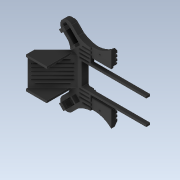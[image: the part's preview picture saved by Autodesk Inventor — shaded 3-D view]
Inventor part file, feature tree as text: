
AUTODESK INVENTOR PART (.ipt)
format: ipt  version: 2020 (Build 240168000, 168)  size: 2,749,440 bytes
history: native  units: mm
features: projected_geometry x46, extrude x34, sketch x34, reference x22, other x20, chamfer x10, plane x4, hole x3, move_body x3, direct_edit x2, emboss x1
ambient origin geometry x8: Origin, YZ Plane, XZ Plane, XY Plane, X Axis, Y Axis, Z Axis, Center Point
bodies: Solid1 (feature_tree)
feature tree (179):
  extrude  "Extrusion1"  Depth=4.404mm
  extrude  "Extrusion2"  Depth=22.0mm
  extrude  "Extrusion3"  Depth=35.3mm
  hole  "Hole2"  [1 undecoded]
  extrude  "Extrusion10"  Depth=19.0mm
  extrude  "Extrusion17"  Depth=10.0mm
  sketch  "Sketch27"  dims[d12=19.0mm d13=100.0mm]
  hole  "Hole4"  [1 undecoded]
  extrude  "Extrusion29"  Depth=17.453293mm
  extrude  "Extrusion30"  Depth=13.962634mm
  extrude  "Extrusion31"  Depth=4.8mm
  extrude  "Extrusion34"  Depth=6.2mm
  plane  "Work Plane1"
  extrude  "Extrusion42"  Depth=2.5mm
  hole  "Hole6"  [1 undecoded]
  extrude  "Extrusion46"  Depth=2.0mm
  chamfer  "Chamfer13"  Distance=2.0mm
  chamfer  "Chamfer14"  Distance=2.0mm
  chamfer  "Chamfer15"  Distance=4.8mm
  chamfer  "Chamfer16"  Distance=33.0mm
  chamfer  "Chamfer17"  Distance=2.5mm
  chamfer  "Chamfer18"  Distance=2.0mm
  extrude  "Extrusion54"  Depth=0.5mm
  chamfer  "Chamfer19"  Distance=2.0mm
  extrude  "Extrusion55"  Depth=14.0mm
  plane  "Work Plane2"
  extrude  "Extrusion57"  Depth=0.5mm
  direct_edit  "Direct Edit5"
  direct_edit  "Direct Edit6"
  plane  "Work Plane3"
  extrude  "Extrusion58"  Depth=0.5mm
  sketch  "Sketch59"  dims[d30=6.2mm]
  extrude  "Extrusion59"  Depth=0.5mm
  extrude  "Extrusion60"  Depth=10.0mm TaperAngle=0.0deg
  chamfer  "Chamfer21"  Distance=146.583126mm
  extrude  "Extrusion61"  Depth=0.5mm
  extrude  "Extrusion62"  Depth=0.5mm
  extrude  "Extrusion63"  Depth=0.5mm
  extrude  "Extrusion64"  Depth=0.5mm
  sketch  "Sketch65"  dims[d37=6.2mm]
  plane  "Work Plane4"
  extrude  "Extrusion65"  Depth=0.5mm
  extrude  "Extrusion66"  Depth=0.5mm
  extrude  "Extrusion68"  Depth=0.5mm
  extrude  "Extrusion69"  Depth=0.5mm
  extrude  "Extrusion71"  Depth=0.5mm
  extrude  "Extrusion84"  Depth=0.5mm
  chamfer  "Chamfer24"  Distance=142.600153mm
  extrude  "Extrusion87"  Depth=0.5mm TaperAngle=0.0deg
  extrude  "Extrusion88"  Depth=5.0mm TaperAngle=0.0deg
  extrude  "Extrusion89"  Depth=5.0mm
  extrude  "Extrusion90"  Depth=0.5mm
  extrude  "Extrusion91"  Depth=0.5mm
  chamfer  "Chamfer25"  Distance=25.0mm
  extrude  "Extrusion93"  Depth=0.5mm TaperAngle=0.0deg
  emboss  "Emboss2"
  extrude  "Extrusion94"  Depth=0.5mm
  sketch  "Sketch1"  dims[d0=50.0mm d1=4.404mm]
  reference  "Reference1"
  reference  "Reference2"
  reference  "Reference3"
  reference  "Reference4"
  sketch  "Sketch2"  dims[d2=135.0deg d3=22.0mm]
  reference  "Reference5"
  reference  "Reference6"
  reference  "Reference7"
  reference  "Reference8"
  reference  "Reference9"
  reference  "Reference10"
  reference  "Reference11"
  reference  "Reference12"
  reference  "Reference13"
  reference  "Reference14"
  reference  "Reference15"
  reference  "Reference16"
  sketch  "Sketch3"  dims[d4=35.3mm d5=35.3mm]
  projected_geometry  "Projected Loop1"
  projected_geometry  "Projected Loop2"
  sketch  "Sketch6"  dims[d6=98.287843mm d7=10.0mm]
  reference  "Reference23"
  reference  "Reference24"
  reference  "Reference25"
  reference  "Reference26"
  reference  "Reference27"
  reference  "Reference28"
  sketch  "Sketch13"  dims[d8=19.0mm d9=19.0mm]
  sketch  "Sketch18"  dims[d10=6.0mm d11=10.0mm]
  projected_geometry  "Projected Loop13"
  projected_geometry  "Projected Loop19"
  projected_geometry  "Projected Loop23"
  projected_geometry  "Projected Loop28"
  projected_geometry  "Projected Loop29"
  projected_geometry  "Projected Loop30"
  projected_geometry  "Projected Loop33"
  sketch  "Sketch31"  dims[d14=30.0mm d15=17.453293mm]
  projected_geometry  "Projected Loop34"
  sketch  "Sketch32"  dims[d16=30.0mm d17=13.962634mm]
  projected_geometry  "Projected Loop35"
  projected_geometry  "Projected Loop36"
  projected_geometry  "Projected Loop37"
  projected_geometry  "Projected Loop38"
  projected_geometry  "Projected Loop39"
  projected_geometry  "Projected Loop40"
  projected_geometry  "Projected Loop41"
  projected_geometry  "Projected Loop42"
  projected_geometry  "Projected Loop43"
  projected_geometry  "Projected Loop44"
  projected_geometry  "Projected Loop45"
  projected_geometry  "Projected Loop46"
  sketch  "Sketch35"  dims[d18=2.0mm d19=4.8mm]
  projected_geometry  "Projected Loop52"
  sketch  "Sketch42"  dims[d20=6.2mm d21=6.2mm]
  projected_geometry  "Projected Loop61"
  projected_geometry  "Projected Loop62"
  sketch  "Sketch46"  dims[d22=33.0mm d23=2.5mm]
  sketch  "Sketch54"  dims[d24=2.0mm d25=2.5mm]
  projected_geometry  "Projected Loop74"
  sketch  "Sketch55"  dims[d26=2.0mm d27=2.0mm]
  sketch  "Sketch57"  dims[d28=90.0deg]
  projected_geometry  "Projected Loop76"
  sketch  "Sketch58"  dims[d29=6.2mm]
  projected_geometry  "Projected Loop77"
  projected_geometry  "Projected Loop78"
  sketch  "Sketch60"  dims[d31=33.0mm]
  projected_geometry  "Projected Loop79"
  projected_geometry  "Projected Loop80"
  sketch  "Sketch61"  dims[d32=2.0mm]
  sketch  "Sketch62"  dims[d33=2.5mm]
  projected_geometry  "Projected Loop81"
  sketch  "Sketch63"  dims[d35=2.0mm]
  sketch  "Sketch64"  dims[d36=4.8mm]
  projected_geometry  "Projected Loop82"
  projected_geometry  "Projected Loop83"
  sketch  "Sketch66"  dims[d38=6.2mm]
  sketch  "Sketch68"  dims[d39=33.0mm]
  projected_geometry  "Projected Loop85"
  projected_geometry  "Projected Loop86"
  sketch  "Sketch69"  dims[d40=2.5mm]
  sketch  "Sketch71"  dims[d41=2.0mm]
  projected_geometry  "Projected Loop88"
  sketch  "Sketch85"  dims[d42=2.5mm]
  projected_geometry  "Projected Loop108"
  sketch  "Sketch88"  dims[d43=2.0mm]
  projected_geometry  "Projected Loop110"
  sketch  "Sketch89"  dims[d44=2.0mm]
  projected_geometry  "Projected Loop111"
  projected_geometry  "Projected Loop112"
  projected_geometry  "Projected Loop113"
  sketch  "Sketch92"  dims[d45=2.5mm]
  projected_geometry  "Projected Loop114"
  sketch  "Sketch93"  dims[d46=19.402mm]
  projected_geometry  "Projected Loop115"
  sketch  "Sketch94"  dims[d47=169.440339mm]
  projected_geometry  "Projected Loop116"
  sketch  "Sketch95"  dims[d48=155.440339mm d58=2.0mm d59=2.0mm d71=4.8mm d72=33.0mm d73=2.5mm d74=2.0mm d75=2.5mm d76=2.0mm d77=14.0mm d78=2.0mm d79=106.731156mm d80=94.331156mm d81=10.0mm d82=0.0mm d83=146.583126mm d84=113.583126mm d85=207.691804mm d86=235.691804mm d87=89.108678mm d88=12.4mm d89=56.108678mm d90=12.4mm d91=23.0mm d92=142.600153mm d93=170.600153mm d94=142.600153mm d95=19.0mm d96=0.0mm d97=5.0mm d98=0.0mm d153=11.0mm d154=6.0mm d155=4.0mm d156=2.0mm d157=90.0deg d158=3.8mm d159=0.0mm d207=5.0mm d208=22.5mm d209=45.0mm d210=25.0mm d211=0.0mm d310=9.0mm d311=0.0mm d382=2.0mm d383=6.0mm d384=4.0mm d385=2.0mm d386=90.0deg d387=10.0mm d388=0.0mm d455=6.0mm d456=4.5mm d457=4.5mm d458=1.7mm d459=12.4mm d460=6.0mm d461=4.5mm d462=4.5mm d463=6.0mm d464=4.5mm d465=4.5mm d466=6.0mm d467=4.5mm d468=4.5mm d472=6.0mm d473=4.5mm d474=4.5mm d475=4.5mm d476=4.5mm d477=6.0mm d478=154.585126mm d479=147.583126mm d480=147.583126mm d481=9.0mm d482=0.0mm d483=154.585126mm d484=90.108678mm d485=10.7mm d486=147.583126mm d487=66.300077mm d488=72.372447mm d489=10.0mm d490=0.0mm d491=0.0mm d492=231.691804mm d493=91.808678mm d494=139.883126mm d495=171.600153mm d496=1.7mm d497=5.0mm d498=0.0mm d523=138.2mm d524=45.2mm d525=22.6mm d526=69.1mm d529=10.0mm d530=0.0mm d590=8.0mm d591=0.0mm d592=2.0mm d593=6.0mm d594=4.0mm d595=2.0mm d596=90.0deg d597=6.5mm d598=0.0mm d669=2.4mm d670=0.0mm d696=4.75mm d697=10.0mm d698=45.0deg d699=4.75mm d700=10.0mm d701=45.0deg d702=4.75mm d703=10.0mm d704=45.0deg d705=4.75mm d706=10.0mm d707=45.0deg d708=4.75mm d709=10.0mm d710=45.0deg d711=4.75mm d712=10.0mm d713=45.0deg d716=4.0mm d717=91.5mm d718=0.0mm d721=2.0mm d722=2.0mm d723=45.0deg d725=5.0mm d726=0.0mm d729=70.0mm d730=135.0deg d731=30.0deg d732=17.3mm d733=135.0deg d734=55.0mm d735=0.0mm d757=0.0mm d758=0.0mm d759=4.0mm d760=0.0mm d761=0.0mm d762=4.0mm d763=0.0mm d764=0.0mm d765=3.025mm d766=0.0mm d767=4.0mm d768=4.0mm d769=40.876479mm d770=46.75mm d771=0.0mm d772=103.75mm d773=0.0mm d774=206.25mm d775=0.0mm d776=4.0mm d777=2.0mm d778=45.0deg d779=12.0mm d780=4.0mm d781=120.0mm d782=15.0mm d785=120.0mm d786=12.0mm d787=15.0mm d788=41.75mm d789=0.0mm d790=3.0mm d791=0.0mm d792=3.0mm d794=3.0mm d795=3.0mm d796=8.0mm d797=0.0mm d805=4.0mm d806=0.0mm d807=0.2mm d808=0.2mm d809=0.2mm d810=0.2mm d811=46.75mm d812=0.0mm d813=63.0mm d814=0.0mm d847=3.7mm d848=3.7mm d849=3.7mm d850=3.7mm d851=3.7mm d852=3.7mm d853=50.0mm d854=50.0mm d855=50.0mm d856=50.0mm d857=10.0mm d858=0.0mm d859=10.0mm d860=0.0mm d867=10.0mm d868=0.0mm d931=5.0mm d932=0.0mm d941=5.0mm d942=2.0mm d943=45.0deg d954=10.0mm d955=0.0mm d956=7.0mm d957=7.0mm d958=7.0mm d959=7.0mm d960=2.0mm d961=0.0mm d962=15.75mm d963=17.5mm d964=0.0mm d965=0.0mm d966=3.5mm d967=0.0mm d968=2.2mm d969=3.0mm d970=72.0mm d971=3.0mm d972=4.0mm d973=16.0mm d974=3.0mm d975=4.0mm d976=3.0mm d977=3.0mm d978=4.0mm d979=3.0mm d980=17.0mm d981=90.0deg d982=3.0mm d983=2.0mm d984=4.0mm d985=3.0mm d986=5.0mm d987=4.0mm d988=10.0mm d989=3.0mm d990=15.0mm d991=3.0mm d992=4.0mm d993=7.0mm d994=3.0mm d995=1.0mm d996=4.0mm d997=5.0mm d998=3.0mm d999=4.0mm d1000=2.0mm d1001=3.0mm d1002=3.0mm d1003=0.5mm d1004=3.0mm d1005=4.0mm d1006=1.5mm d1007=3.0mm d1008=0.5mm d1009=0.5mm d1010=3.0mm d1011=0.0mm d1012=1.0mm d1013=2.0mm d1014=45.0deg d1015=3.2mm d1016=21.0mm d1017=3.0mm d1018=4.0mm d1019=3.0mm d1020=4.0mm d1021=3.0mm d1022=4.0mm d1023=15.0mm d1024=3.0mm d1025=3.0mm d1030=1.501978mm d1031=113.9mm d1032=131.9mm d1033=132.077604mm d1034=59.4mm d1035=110.9mm d1036=62.4mm d1037=110.9mm d1038=66.4mm d1039=110.9mm d1040=69.4mm d1041=110.9mm d1042=73.4mm d1043=110.9mm d1044=76.4mm d1045=110.9mm d1046=3.0mm d1047=0.0mm d1048=4.0mm d1049=3.0mm d1050=4.0mm d1051=3.0mm d1052=4.0mm d1053=3.0mm d1054=4.0mm d1055=3.0mm d1056=4.0mm d1057=3.0mm d1058=5.515mm d1059=58.97mm d1062=5.0mm d1063=5.0mm d1064=5.0mm d1065=5.0mm d1066=5.0mm d1067=0.0mm d1068=5.515mm d1069=10.515mm d1070=46.488mm d1071=8.512mm d1072=64.485mm d1073=10.515mm d1074=13.4mm d1075=13.4mm d1076=3.0mm d1077=3.0mm d1078=58.8mm d1079=3.0mm d1080=26.8mm d1081=3.0mm d1082=15.0mm d1083=0.0mm d99=0.5mm d100=0.872665mm d160=0.5mm d161=0.872665mm d162=0.5mm d163=0.872665mm d171=0.5mm d172=0.872665mm d173=0.5mm d174=0.872665mm d191=0.5mm d192=0.872665mm d193=0.5mm d194=0.872665mm d205=0.5mm d206=0.872665mm d244=0.5mm d245=0.872665mm d246=0.5mm d247=0.872665mm d307=0.5mm d308=0.872665mm d309=0.5mm d352=0.5mm d353=0.872665mm d354=0.5mm d355=0.872665mm d412=0.5mm d413=0.872665mm d414=0.5mm d415=0.872665mm d416=0.5mm d417=0.872665mm d586=0.5mm d587=0.872665mm d588=0.5mm d589=0.872665mm d861=0.5mm d862=0.872665mm d905=0.5mm d906=0.872665mm d907=0.5mm d908=0.872665mm d950=0.5mm d951=0.872665mm d952=0.5mm d953=0.872665mm]
  projected_geometry  "Projected Loop117"
  other  "<userpath>\Documents\Inventor Projects\SpiderTest\Test3\SpiderLegDemo.iam"
  other  "SpiderLegDemo.iam"
  other  "Tower Pro MG90S Micro servo:1"
  other  "Крышка корпуса задняя:1"
  other  "Крышка корпуса:1"
  other  "LegSup:1"
  other  "<userpath>\Documents\Inventor Projects\SpiderTest\Test5\Demo.iam"
  other  "Demo.iam"
  other  "SpiderLegDemoRight:1"
  other  "SpiderLegDemoRight:5"
  other  "<userpath>\Documents\Inventor Projects\SpiderTest\Test3\Demo.iam"
  other  "SpiderLegDemo:3"
  other  "SpiderLegDemo:4"
  other  "SpiderLegDemo:2"
  other  "SpiderLegDemoRight:6"
  other  "SpiderLegDemoLeft:2"
  other  "Вал последний с чем то:1"
  other  "SpiderLegDemoLeft:3"
  other  "ограничитель:2"
  other  "SpiderLegDemoLeft:1"
  move_body  "Move7"
  move_body  "Move8"
  move_body  "Move9"
note: 3 required parameter values undecoded (feature->parameter linkage not recoverable at this tier; creation-order binding heuristic only, values carry confidence <= 0.55)
